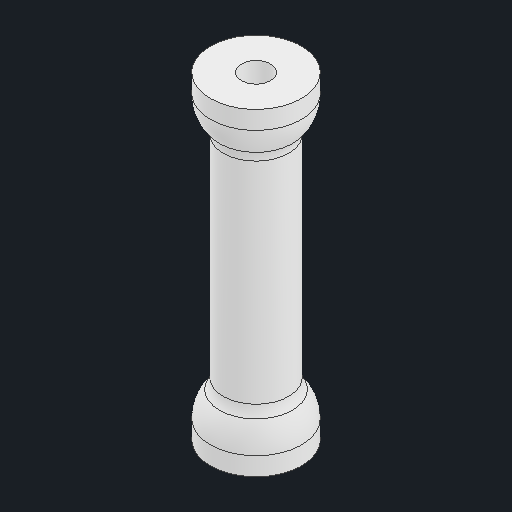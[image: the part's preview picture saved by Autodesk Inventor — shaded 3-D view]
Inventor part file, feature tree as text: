
AUTODESK INVENTOR PART (.ipt)
format: ipt  version: 2024.3 (Build 283343010, 343A)  size: 147,968 bytes
history: native  units: in
note: dims shown in document units (in); Inventor stores cm internally (conversion verified against a paired STEP export)
features: revolve x1, mirror x1, sketch x1
ambient origin geometry x8: Origin, YZ Plane, XZ Plane, XY Plane, X Axis, Y Axis, Z Axis, Center Point
bodies: Solid1 (feature_tree)
feature tree (3):
  revolve  "Revolution1"  [1 undecoded]
  mirror  "Mirror1"
  sketch  "Sketch1"  dims[d0=0.1in d2=1.0938in d3=0.125in d5=0.125in d6=0.3in d8=90.0deg d9=0.3125in d10=0.0625in]
note: 1 required parameter value undecoded (feature->parameter linkage not recoverable at this tier; creation-order binding heuristic only, values carry confidence <= 0.55)
